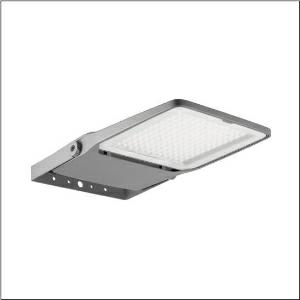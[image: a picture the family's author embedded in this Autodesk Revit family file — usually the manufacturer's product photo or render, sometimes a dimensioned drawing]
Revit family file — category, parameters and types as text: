
# Revit family: floodlight_fl_20_midi___pl43_5xa7682e3a2ac_3a80
name_source: partatom
category: Lighting Fixtures
units: mm (PartAtom-declared; Revit-internal decimal feet)

## family parameters
Cut with Voids When Loaded = No
Host = Face
Light Source = No
Part Type = Normal
Room Calculation Point = No
Round Connector Dimension = Use Diameter
Shared = No

## types (1)
- --- (1 x LED 5000K / CRI = 70 (unbekannt), 28900 lm, 5000K)
    Apparent Load = 208 VA
    CIE Flux Codes = 32 74 99 100 100
    Color Rendering = 70
    Color Temperature = 5000K
    Default Elevation = 1800 mm
    Description = Floodlight FL 20 midi, floodlight, primary light control with lens, of plastic, primary optical cover: protective disc, of toughened safety glass, transparent, light distribution: PL43, light emission: direct distribution, primary light characteristic: asymmetric, installation type: surface-mounted, LED High Power LED, rated luminous flux: 28.900 lm, light colour: 750, colour temperature: 5000K, control gear: ECG Plus, control: flexible luminous flux parameterisation, time-dependent luminous flux control, digital communication interface, power reduction, overheat protection, electronic power reduction, with terminal, 5-pole, max. 2.5mm², mains connection: 220..240V, AC, 50/60Hz, rated input power: 208W, LED unit, of diecast aluminium, powder-coated, Siteco® metallic grey (DB 702S), length: 731 mm, width: 450 mm, height: 76mm, housing frame, of diecast aluminium, powder-coated, Siteco® metallic grey (DB 702S), wall fastening, of steel, powder-coated, Siteco® metallic grey (DB 702S), DALIprotection rating (complete): IP66, insulation class (complete): insulation class II (safety insulation), certification: CE, ENEC, VDE, protection symbol: D, permissible ambient temperature for indoor applications: -40..+40°C, permissible ambient temperature for outdoor applications: -40..+50°C, standard: DIN EN 12944, packaging unit: 1 piece

Light Distribution: PL43
    Height = 76 mm
    Lamp = 1 x LED 5000K / CRI >= 70 (unbekannt)
    Lamp Light Flux = 28900 lm
    Lamp count = 1
    Length = 731 mm
    Luminous efficacy = 139 lm/W
    Manufacturer = Siteco
    ModVariant = No
    Model = 5XA7682E3A2AC
    Number of Poles = 1
    OnlyDefault = Yes
    Power Factor = 1
    Product Name = Floodlight FL 20 midi | PL43
    Product group = floodlight | pylon top
    ProductGroupID = 6101
    Protection Class = Protection class II
    Protection Degree = IP 66
    RLX_Detail_Level = 1
    RlxData = <blob elided: 91637 chars, md5=37be4b70>
    Socket = socket
    Standby Power = 0 W
    System Light Flux = 28900 lm
    System Power = 208 W
    Type Comments = factory setting: luminous flux: 100 % | dim-lin: 254 | 484 mA
    Type Image = l_1005944.jpg
    URL = http://relux.com
    VarID = @adj_143549
    Voltage = 0 V
    Weight = 0.00 kg
    Width = 450 mm

## geometry (parser evidence)
native form markers: Blend x4, Sweep x13
no freeform markers — native parametric forms only
